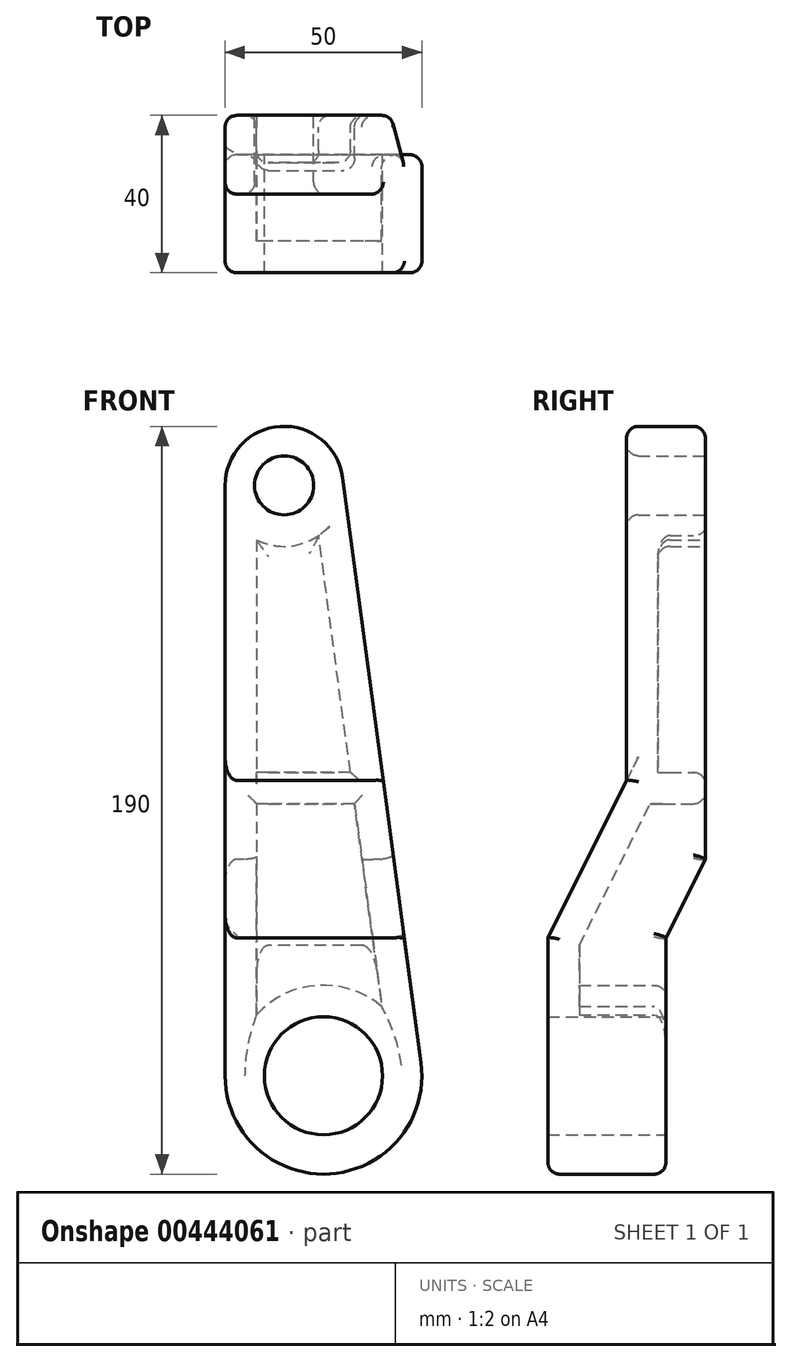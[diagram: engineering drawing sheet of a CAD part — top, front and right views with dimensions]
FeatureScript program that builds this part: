
annotation { "Feature Type Name" : "Feature", "Feature Type Description" : "" }
export const myFeature = defineFeature(function(context is Context, id is Id, definition is map)
    precondition{}
    {
        {
            var Q0;
            Q0=qCreatedBy(makeId("Front.planeOp"),FACE);
            var sketch = newSketch(context, id + "F0", { "sketchPlane" : qUnion([Q0])});
            skCircle(sketch, "E0", {"center": v(0, 0) * mm, "radius": 25 * mm});
            skCircle(sketch, "E1", {"center": v(-10, 150) * mm, "radius": 15 * mm});
            skLineSegment(sketch, "E2", {"start": v(-25, 150) * mm, "end": v(-25, 0) * mm});
            skLineSegment(sketch, "E3", {"start": v(4.87, 152) * mm, "end": v(24.78, 3.32) * mm});
            skSolve(sketch);
        }
        {
            var Q0;
            Q0 = qSketchRegion(id + "F0", true);
            extrude(context, id + "F1", {"entities" : qUnion([Q0]), "depth" : 40 * mm});
        }
        {
            var Q0;
            Q0=makeQuery(id+"F1.opExtrude","SWEPT_FACE",FACE,{"disambiguationData":[OSD([sQuery(id+"F0.wireOp",EDGE,"E2")])]});
            var sketch = newSketch(context, id + "F2", { "sketchPlane" : qUnion([Q0])});
            skLineSegment(sketch, "E4", {"start": v(0, 55) * mm, "end": v(0, -25.94) * mm});
            skLineSegment(sketch, "E5", {"start": v(10, -25.94) * mm, "end": v(10, 35) * mm});
            skLineSegment(sketch, "E6", {"start": v(10, 35) * mm, "end": v(0, 55) * mm});
            skLineSegment(sketch, "E7", {"start": v(40, 35) * mm, "end": v(40, 165.97) * mm});
            skLineSegment(sketch, "E8", {"start": v(20, 165.97) * mm, "end": v(20, 75) * mm});
            skLineSegment(sketch, "E9", {"start": v(20, 75) * mm, "end": v(40, 35) * mm});
            skLineSegment(sketch, "E10", {"start": v(0, -25.94) * mm, "end": v(10, -25.94) * mm});
            skLineSegment(sketch, "E11", {"start": v(20, 165.97) * mm, "end": v(40, 165.97) * mm});
            skSolve(sketch);
        }
        {
            var Q0;
            {var subQ4=sQuery(id+"F2.wireOp",EDGE,"E9");Q0=makeQuery(id+"F2.imprint","IMPRINT",FACE,{"disambiguationData":[TD([[makeQuery(id+"F2.imprint","IMPRINT",EDGE,{"derivedFrom":subQ4}),1.0]])]});}
            var Q1;
            {var subQ3=sQuery(id+"F2.wireOp",EDGE,"DIlLD0Hy-IEWM-XMB4-UN3K-K1qchYSTCbxG");Q1=makeQuery(id+"F2.imprint","IMPRINT",FACE,{"disambiguationData":[TD([[makeQuery(id+"F2.imprint","IMPRINT",EDGE,{"derivedFrom":subQ3}),1.0]])]});}
            var Q2;
            {var subQ3=sQuery(id+"F2.wireOp",EDGE,"5LHhSn52-8Qpd-DfJ1-nUde-YrkTcAlSUMm7");Q2=makeQuery(id+"F2.imprint","IMPRINT",FACE,{"disambiguationData":[TD([[makeQuery(id+"F2.imprint","IMPRINT",EDGE,{"derivedFrom":subQ3}),1.0]])]});}
            var Q3;
            {var subQ3=sQuery(id+"F2.wireOp",EDGE,"E11");Q3=makeQuery(id+"F2.imprint","IMPRINT",FACE,{"disambiguationData":[TD([[makeQuery(id+"F2.imprint","IMPRINT",EDGE,{"derivedFrom":subQ3}),-1.0]])]});}
            var Q4;
            {var subQ4=sQuery(id+"F2.wireOp",EDGE,"E6");Q4=makeQuery(id+"F2.imprint","IMPRINT",FACE,{"disambiguationData":[TD([[makeQuery(id+"F2.imprint","IMPRINT",EDGE,{"derivedFrom":subQ4}),1.0]])]});}
            var Q5;
            {var subQ3=sQuery(id+"F2.wireOp",EDGE,"E10");Q5=makeQuery(id+"F2.imprint","IMPRINT",FACE,{"disambiguationData":[TD([[makeQuery(id+"F2.imprint","IMPRINT",EDGE,{"derivedFrom":subQ3}),1.0]])]});}
            extrude(context, id + "F3", {"entities" : qUnion([Q0, Q1, Q2, Q3, Q4, Q5]), "operationType" : NewBodyOperationType.REMOVE, "endBound" : BoundingType.THROUGH_ALL, "oppositeDirection" : true, "depth" : 25 * mm});
        }
        {
            var Q0;
            Q0=makeQuery(id+"F1.opExtrude","CAP_FACE",FACE,{"disambiguationData":[OSD([sQuery(id+"F0.wireOp",EDGE,"E0"),sQuery(id+"F0.wireOp",EDGE,"E1"),sQuery(id+"F0.wireOp",EDGE,"E2"),sQuery(id+"F0.wireOp",EDGE,"E3")])],"isStart":true});
            var sketch = newSketch(context, id + "F4", { "sketchPlane" : qUnion([Q0])});
            skCircle(sketch, "E12", {"center": v(0, 0) * mm, "radius": 15 * mm});
            skCircle(sketch, "E13", {"center": v(10, 150) * mm, "radius": 7.5 * mm});
            skSolve(sketch);
        }
        {
            var Q0;
            Q0=makeQuery(id+"F4.imprint","IMPRINT",FACE,{"disambiguationData":[TD([[makeQuery(id+"F4.imprint","IMPRINT",EDGE,{"derivedFrom":sQuery(id+"F4.wireOp",EDGE,"E13")}),1.0]])]});
            var Q1;
            Q1=makeQuery(id+"F4.imprint","IMPRINT",FACE,{"disambiguationData":[TD([[makeQuery(id+"F4.imprint","IMPRINT",EDGE,{"derivedFrom":sQuery(id+"F4.wireOp",EDGE,"E12")}),1.0]])]});
            var Q2;
            Q2=sQuery(id+"F4.wireOp",EDGE,"E13");
            var Q3;
            Q3=sQuery(id+"F4.wireOp",EDGE,"E12");
            extrude(context, id + "F5", {"entities" : qUnion([Q0, Q1]), "operationType" : NewBodyOperationType.REMOVE, "surfaceEntities" : qUnion([Q2, Q3]), "endBound" : BoundingType.THROUGH_ALL, "oppositeDirection" : true, "depth" : 25 * mm});
        }
        {
            var Q0;
            Q0=makeQuery(id+"F1.opExtrude","CAP_FACE",FACE,{"disambiguationData":[OSD([sQuery(id+"F0.wireOp",EDGE,"E0"),sQuery(id+"F0.wireOp",EDGE,"E1"),sQuery(id+"F0.wireOp",EDGE,"E2"),sQuery(id+"F0.wireOp",EDGE,"E3")])],"isStart":true});
            var Q1;
            Q1=makeQuery(id+"F3.boolean.opBoolean","COPY",FACE,{"derivedFrom":makeQuery(id+"F3.opExtrude","SWEPT_FACE",FACE,{"disambiguationData":[OSD([sQuery(id+"F2.wireOp",EDGE,"E6")])]})});
            var Q2;
            Q2=makeQuery(id+"F3.boolean.opBoolean","COPY",FACE,{"derivedFrom":makeQuery(id+"F3.opExtrude","SWEPT_FACE",FACE,{"disambiguationData":[OSD([sQuery(id+"F2.wireOp",EDGE,"E5")])]})});
            shell(context, id + "F6", {"entities" : qUnion([Q0, Q1, Q2]), "thickness" : 8 * mm});
        }
        {
            var Q0;
            Q0=makeQuery(id+"F1.opExtrude","CAP_FACE",FACE,{"disambiguationData":[OSD([sQuery(id+"F0.wireOp",EDGE,"E0"),sQuery(id+"F0.wireOp",EDGE,"E1"),sQuery(id+"F0.wireOp",EDGE,"E2"),sQuery(id+"F0.wireOp",EDGE,"E3")])],"isStart":true});
            var sketch = newSketch(context, id + "F7", { "sketchPlane" : qUnion([Q0])});
            skLineSegment(sketch, "E14", {"start": v(-6.82, 77.11) * mm, "end": v(17, 77.11) * mm});
            skLineSegment(sketch, "E15", {"start": v(-7.9, 69.11) * mm, "end": v(17, 69.11) * mm});
            skLineSegment(sketch, "E16.0", {"start": v(-6.82, 77.11) * mm, "end": v(-7.9, 69.11) * mm});
            skLineSegment(sketch, "E17.0", {"start": v(17, 77.11) * mm, "end": v(17, 69.11) * mm});
            skPoint(sketch, "E18.orphan", {"position": v(1.23, 137.22) * mm});
            skPoint(sketch, "E19.orphan", {"position": v(-9.79, 55) * mm});
            skPoint(sketch, "E20.orphan", {"position": v(17, 55) * mm});
            skPoint(sketch, "E21.orphan", {"position": v(17, 136.17) * mm});
            skSolve(sketch);
        }
        {
            var Q0;
            Q0 = qSketchRegion(id + "F7", true);
            extrude(context, id + "F8", {"entities" : qUnion([Q0]), "operationType" : NewBodyOperationType.ADD, "endBound" : BoundingType.UP_TO_NEXT, "oppositeDirection" : true, "depth" : 25 * mm});
        }
        {
            var Q0;
            Q0=makeQuery(id+"F1.opExtrude","CAP_EDGE",EDGE,{"disambiguationData":[OSD([sQuery(id+"F0.wireOp",EDGE,"E1")])],"isStart":true});
            var Q1;
            Q1=makeQuery(id+"F5.boolean.opBoolean","COPY",EDGE,{"derivedFrom":makeQuery(id+"F5.opExtrude","CAP_EDGE",EDGE,{"disambiguationData":[OSD([sQuery(id+"F4.wireOp",EDGE,"E13")])],"isStart":true})});
            var Q2;
            Q2=makeQuery(id+"F5.boolean.opBoolean","INTERSECT",EDGE,{"derivedFrom":[makeQuery(id+"F3.boolean.opBoolean","COPY",FACE,{"derivedFrom":makeQuery(id+"F3.opExtrude","SWEPT_FACE",FACE,{"disambiguationData":[OSD([sQuery(id+"F2.wireOp",EDGE,"E8")])]})}),makeQuery(id+"F5.opExtrude","SWEPT_FACE",FACE,{"disambiguationData":[OSD([sQuery(id+"F4.wireOp",EDGE,"E13")])]})]});
            var Q3;
            Q3=makeQuery(id+"F1.opExtrude","CAP_EDGE",EDGE,{"disambiguationData":[OSD([sQuery(id+"F0.wireOp",EDGE,"E3")])],"isStart":true});
            var Q4;
            {var subQ0=sQuery(id+"F0.wireOp",EDGE,"E3");Q4=makeQuery(id+"F8.boolean.opBoolean","SPLIT",EDGE,{"disambiguationData":[TD([makeQuery(id+"F6.opShell","OFFSET_FACE",FACE,{"disambiguationData":[OSD([sQuery(id+"F4.wireOp",EDGE,"E13")])]})])],"derivedFrom":makeQuery(id+"F6.opShell","OFFSET_EDGE",EDGE,{"disambiguationData":[OSD([subQ0]),TDD([makeQuery(id+"F1.opExtrude","CAP_EDGE",EDGE,{"disambiguationData":[OSD([subQ0])],"isStart":true})])]})});}
            var Q5;
            Q5=makeQuery(id+"F6.opShell","OFFSET_EDGE",EDGE,{"disambiguationData":[OSD([sQuery(id+"F2.wireOp",EDGE,"E8")])]});
            var Q6;
            Q6=makeQuery(id+"F6.opShell","OFFSET_EDGE",EDGE,{"disambiguationData":[OSD([sQuery(id+"F4.wireOp",EDGE,"E13")])]});
            var Q7;
            Q7=makeQuery(id+"F8.opExtrude","CAP_EDGE",EDGE,{"disambiguationData":[OSD([sQuery(id+"F7.wireOp",EDGE,"E14")])],"isStart":true});
            var Q8;
            Q8=makeQuery(id+"F1.opExtrude","CAP_EDGE",EDGE,{"disambiguationData":[OSD([sQuery(id+"F0.wireOp",EDGE,"E2")])],"isStart":true});
            var Q9;
            Q9=makeQuery(id+"F3.boolean.opBoolean","COPY",EDGE,{"derivedFrom":makeQuery(id+"F3.opExtrude","CAP_EDGE",EDGE,{"disambiguationData":[OSD([sQuery(id+"F2.wireOp",EDGE,"E5")])],"isStart":true})});
            var Q10;
            Q10=makeQuery(id+"F3.boolean.opBoolean","INTERSECT",EDGE,{"derivedFrom":[makeQuery(id+"F1.opExtrude","SWEPT_FACE",FACE,{"disambiguationData":[OSD([sQuery(id+"F0.wireOp",EDGE,"E0")])]}),makeQuery(id+"F3.opExtrude","SWEPT_FACE",FACE,{"disambiguationData":[OSD([sQuery(id+"F2.wireOp",EDGE,"E5")])]})]});
            var Q11;
            Q11=makeQuery(id+"F3.boolean.opBoolean","INTERSECT",EDGE,{"derivedFrom":[makeQuery(id+"F1.opExtrude","SWEPT_FACE",FACE,{"disambiguationData":[OSD([sQuery(id+"F0.wireOp",EDGE,"E3")])]}),makeQuery(id+"F3.opExtrude","SWEPT_FACE",FACE,{"disambiguationData":[OSD([sQuery(id+"F2.wireOp",EDGE,"E5")])]})]});
            var Q12;
            Q12=makeQuery(id+"F3.boolean.opBoolean","INTERSECT",EDGE,{"derivedFrom":[makeQuery(id+"F1.opExtrude","SWEPT_FACE",FACE,{"disambiguationData":[OSD([sQuery(id+"F0.wireOp",EDGE,"E3")])]}),makeQuery(id+"F3.opExtrude","SWEPT_FACE",FACE,{"disambiguationData":[OSD([sQuery(id+"F2.wireOp",EDGE,"E6")])]})]});
            var Q13;
            Q13=makeQuery(id+"F6.opShell","OFFSET_EDGE",EDGE,{"disambiguationData":[OSD([sQuery(id+"F0.wireOp",EDGE,"E3"),sQuery(id+"F2.wireOp",EDGE,"E6")])]});
            var Q14;
            {var subQ1=sQuery(id+"F0.wireOp",EDGE,"E3");Q14=makeQuery(id+"F8.boolean.opBoolean","SPLIT",EDGE,{"disambiguationData":[TD([makeQuery(id+"F6.opShell","OFFSET_FACE",FACE,{"disambiguationData":[OSD([sQuery(id+"F2.wireOp",EDGE,"E6")])]})])],"derivedFrom":makeQuery(id+"F6.opShell","OFFSET_EDGE",EDGE,{"disambiguationData":[OSD([subQ1]),TDD([makeQuery(id+"F1.opExtrude","CAP_EDGE",EDGE,{"disambiguationData":[OSD([subQ1])],"isStart":true})])]})});}
            var Q15;
            Q15=makeQuery(id+"F8.opExtrude","CAP_EDGE",EDGE,{"disambiguationData":[OSD([sQuery(id+"F7.wireOp",EDGE,"E15")])],"isStart":true});
            var Q16;
            {var subQ0=sQuery(id+"F0.wireOp",EDGE,"E2");Q16=makeQuery(id+"F8.boolean.opBoolean","SPLIT",EDGE,{"disambiguationData":[TD([makeQuery(id+"F3.boolean.opBoolean","COPY",FACE,{"derivedFrom":makeQuery(id+"F3.opExtrude","SWEPT_FACE",FACE,{"disambiguationData":[OSD([sQuery(id+"F2.wireOp",EDGE,"E6")])]})})])],"derivedFrom":makeQuery(id+"F6.opShell","OFFSET_EDGE",EDGE,{"disambiguationData":[OSD([subQ0]),TDD([makeQuery(id+"F1.opExtrude","CAP_EDGE",EDGE,{"disambiguationData":[OSD([subQ0])],"isStart":true})])]})});}
            var Q17;
            Q17=makeQuery(id+"F6.opShell","OFFSET_EDGE",EDGE,{"disambiguationData":[OSD([sQuery(id+"F2.wireOp",EDGE,"E9")])]});
            var Q18;
            Q18=makeQuery(id+"F6.opShell","OFFSET_EDGE",EDGE,{"disambiguationData":[OSD([sQuery(id+"F2.wireOp",EDGE,"E5")])]});
            var Q19;
            Q19=makeQuery(id+"F6.opShell","OFFSET_EDGE",EDGE,{"disambiguationData":[OSD([sQuery(id+"F2.wireOp",EDGE,"E5"),sQuery(id+"F4.wireOp",EDGE,"E12")])]});
            var Q20;
            Q20=makeQuery(id+"F6.opShell","OFFSET_EDGE",EDGE,{"disambiguationData":[OSD([sQuery(id+"F0.wireOp",EDGE,"E3"),sQuery(id+"F2.wireOp",EDGE,"E5")])]});
            var Q21;
            Q21=makeQuery(id+"F6.opShell","OFFSET_EDGE",EDGE,{"disambiguationData":[OSD([sQuery(id+"F2.wireOp",EDGE,"E6")])]});
            var Q22;
            Q22=makeQuery(id+"F3.boolean.opBoolean","COPY",EDGE,{"derivedFrom":makeQuery(id+"F3.opExtrude","CAP_EDGE",EDGE,{"disambiguationData":[OSD([sQuery(id+"F2.wireOp",EDGE,"E6")])],"isStart":true})});
            var Q23;
            Q23=makeQuery(id+"F3.boolean.opBoolean","COPY",EDGE,{"derivedFrom":makeQuery(id+"F3.opExtrude","CAP_EDGE",EDGE,{"disambiguationData":[OSD([sQuery(id+"F2.wireOp",EDGE,"E8")])],"isStart":true})});
            var Q24;
            Q24=makeQuery(id+"F3.boolean.opBoolean","INTERSECT",EDGE,{"derivedFrom":[makeQuery(id+"F1.opExtrude","SWEPT_FACE",FACE,{"disambiguationData":[OSD([sQuery(id+"F0.wireOp",EDGE,"E3")])]}),makeQuery(id+"F3.opExtrude","SWEPT_FACE",FACE,{"disambiguationData":[OSD([sQuery(id+"F2.wireOp",EDGE,"E8")])]})]});
            var Q25;
            Q25=makeQuery(id+"F3.boolean.opBoolean","INTERSECT",EDGE,{"derivedFrom":[makeQuery(id+"F1.opExtrude","SWEPT_FACE",FACE,{"disambiguationData":[OSD([sQuery(id+"F0.wireOp",EDGE,"E1")])]}),makeQuery(id+"F3.opExtrude","SWEPT_FACE",FACE,{"disambiguationData":[OSD([sQuery(id+"F2.wireOp",EDGE,"E8")])]})]});
            var Q26;
            Q26=makeQuery(id+"F1.opExtrude","CAP_EDGE",EDGE,{"disambiguationData":[OSD([sQuery(id+"F0.wireOp",EDGE,"E0")])],"isStart":false});
            var Q27;
            Q27=makeQuery(id+"F1.opExtrude","CAP_EDGE",EDGE,{"disambiguationData":[OSD([sQuery(id+"F0.wireOp",EDGE,"E3")])],"isStart":false});
            var Q28;
            Q28=makeQuery(id+"F3.boolean.opBoolean","INTERSECT",EDGE,{"derivedFrom":[makeQuery(id+"F1.opExtrude","SWEPT_FACE",FACE,{"disambiguationData":[OSD([sQuery(id+"F0.wireOp",EDGE,"E3")])]}),makeQuery(id+"F3.opExtrude","SWEPT_FACE",FACE,{"disambiguationData":[OSD([sQuery(id+"F2.wireOp",EDGE,"E9")])]})]});
            var Q29;
            Q29=makeQuery(id+"F3.boolean.opBoolean","COPY",EDGE,{"derivedFrom":makeQuery(id+"F3.opExtrude","CAP_EDGE",EDGE,{"disambiguationData":[OSD([sQuery(id+"F2.wireOp",EDGE,"E9")])],"isStart":true})});
            var Q30;
            Q30=makeQuery(id+"F1.opExtrude","CAP_EDGE",EDGE,{"disambiguationData":[OSD([sQuery(id+"F0.wireOp",EDGE,"E2")])],"isStart":false});
            fillet(context, id + "F9", {"entities" : qUnion([Q0, Q1, Q2, Q3, Q4, Q5, Q6, Q7, Q8, Q9, Q10, Q11, Q12, Q13, Q14, Q15, Q16, Q17, Q18, Q19, Q20, Q21, Q22, Q23, Q24, Q25, Q26, Q27, Q28, Q29, Q30]), "radius" : 3 * mm, "tangentPropagation" : true, "allowEdgeOverflow" : false});
        }
    });
